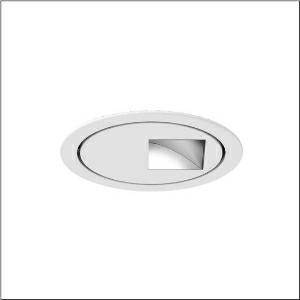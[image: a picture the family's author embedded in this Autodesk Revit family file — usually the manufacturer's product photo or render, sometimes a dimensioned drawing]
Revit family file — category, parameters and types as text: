
# Revit family: lunis_11_mini_round_51dk11cd2wf21
name_source: partatom
category: Lighting Fixtures
units: mm (PartAtom-declared; Revit-internal decimal feet)

## family parameters
Cut with Voids When Loaded = No
Host = Face
Light Source = No
Part Type = Normal
Room Calculation Point = No
Round Connector Dimension = Use Diameter
Shared = No

## types (1)
- Lunis 11 mini round (1 x LED 3000K / CRI = 80 (unbekannt), 2380 lm, 3000K)
    Apparent Load = 28 VA
    CIE Flux Codes = 44 77 97 100 100
    Color Rendering = 80
    Color Temperature = 3000K
    Default Elevation = 1800 mm
    Description = Lunis 11 mini round, downlight, light control with wallwasher, of highly reflective aluminium, highly specular, light emission: direct distribution, LED rated luminous flux: 2.380lm, light colour: 830, control gear: ECG, with terminal, 5-pole, mains connection: 220..230V, AC/DC, 0/50..60Hz, LED module, luminaire module, of aluminium, highly specular, white, diameter: 176mm, clamping range: 1..40mm, recessing ring, of plastic, traffic white (RAL 9016), protection rating (complete): IP20, insulation class (complete): insulation class II (safety insulation), certification: CE, permissible ambient temperature for indoor applications: 0..+35°C, packaging unit: 1 piece
    Height = 0 mm  [stored 0 ft]
    Lamp = 1 x LED 3000K / CRI >= 80 (unbekannt)
    Lamp Light Flux = 2380 lm
    Lamp count = 1
    Length = 176 mm
    Luminous efficacy = 86 lm/W
    Manufacturer = Siteco
    ModVariant = No
    Model = 51DK11CD2WF21
    Mounting Place = Ceiling
    Mounting Type = Recessed
    Number of Poles = 1
    OnlyDefault = Yes
    Power Factor = 1
    Product Name = Lunis 11 mini round
    Product group = downlight
    ProductGroupID = 401
    Protection Class = Protection class II
    Protection Degree = IP 20
    RLX_Detail_Level = 1
    RLX_Emergency_Light_Flux = 0 lm
    RLX_Emergency_Type = 0
    RLX_Emergency_Type_DB = No
    RlxData = <blob elided: 59581 chars, md5=7e902d0d>
    Socket = socket
    Standby Power = 0 W
    System Light Flux = 2380 lm
    System Power = 28 W
    Type Comments = Product without accessories
    Type Image = l_1004772.jpg
    URL = http://relux.com
    VarID = ---
    Voltage = 0 V
    Weight = 0.00 kg
    Width = 176 mm

note: [stored X ft] marks values corroborated as IEEE doubles in the binary element streams (Revit-internal decimal feet)

## geometry (parser evidence)
native form markers: Blend x4, Sweep x12
no freeform markers — native parametric forms only
